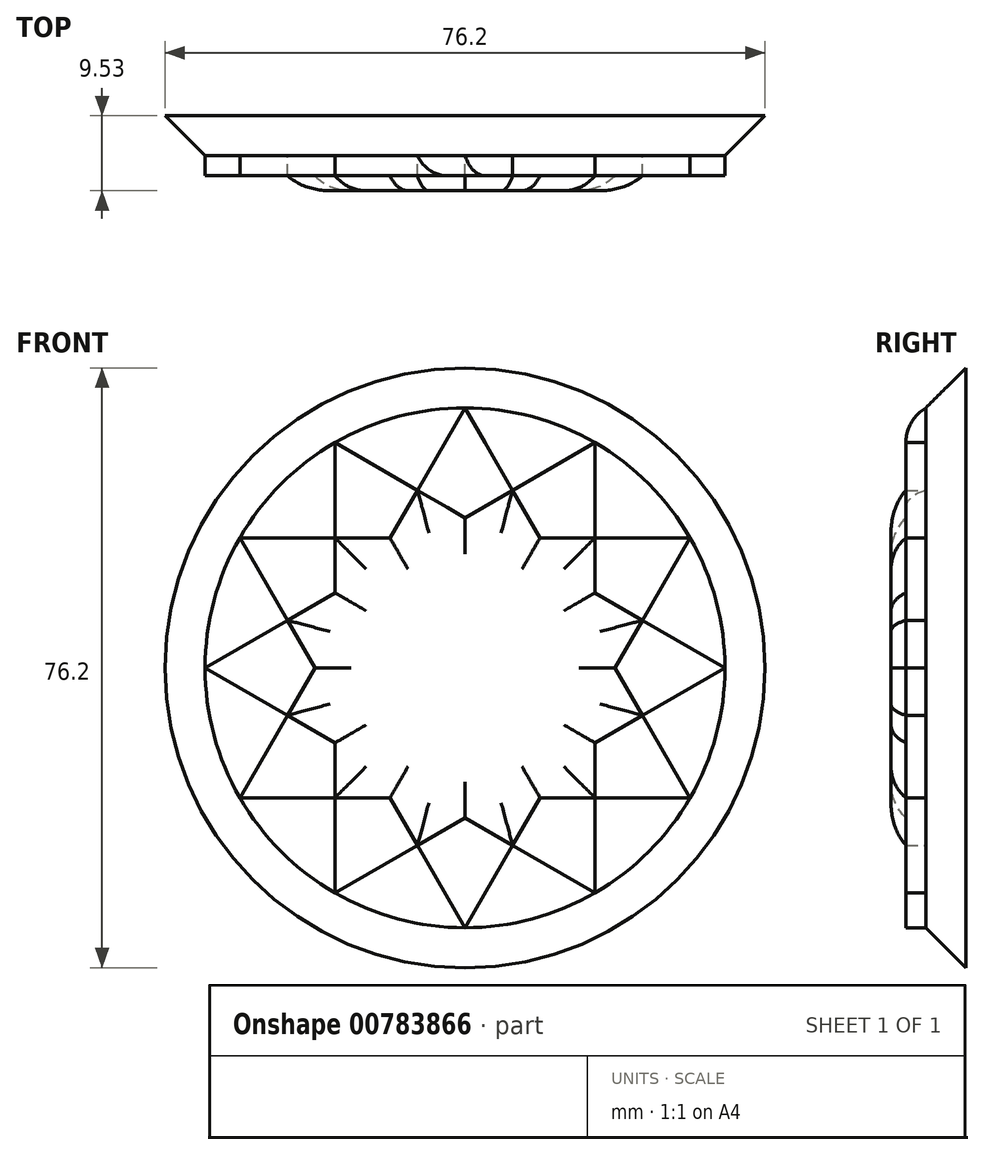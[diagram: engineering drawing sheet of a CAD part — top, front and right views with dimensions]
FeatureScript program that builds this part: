
annotation { "Feature Type Name" : "Feature", "Feature Type Description" : "" }
export const myFeature = defineFeature(function(context is Context, id is Id, definition is map)
    precondition{}
    {
        {
            var Q0;
            Q0=qCreatedBy(makeId("Front.planeOp"),FACE);
            var sketch = newSketch(context, id + "F0", { "sketchPlane" : qUnion([Q0])});
            skCircle(sketch, "E0", {"center": v(0, 0) * mm, "radius": 38.1 * mm});
            skSolve(sketch);
        }
        {
            var Q0;
            Q0=makeQuery(id+"F0.imprint","IMPRINT",FACE,{"disambiguationData":[TD([[makeQuery(id+"F0.imprint","IMPRINT",EDGE,{"derivedFrom":sQuery(id+"F0.wireOp",EDGE,"E0")}),1.0]])]});
            extrude(context, id + "F1", {"entities" : qUnion([Q0]), "depth" : 5.08 * mm, "offsetDistance" : 25.4 * mm});
        }
        {
            var Q0;
            Q0=makeQuery(id+"F1.opExtrude","CAP_EDGE",EDGE,{"disambiguationData":[OSD([sQuery(id+"F0.wireOp",EDGE,"E0")])],"isStart":false});
            chamfer(context, id + "F2", {"entities" : qUnion([Q0]), "width" : 5.08 * mm, "tangentPropagation" : true});
        }
        {
            var Q0;
            Q0=makeQuery(id+"F1.opExtrude","CAP_FACE",FACE,{"disambiguationData":[OSD([sQuery(id+"F0.wireOp",EDGE,"E0")])],"isStart":false});
            var sketch = newSketch(context, id + "F3", { "sketchPlane" : qUnion([Q0])});
            skCircle(sketch, "E1.cCircle", {"center": v(0, 0) * mm, "radius": 33.02 * mm, "construction": true});
            skLineSegment(sketch, "E1.0", {"start": v(0, 33.02) * mm, "end": v(28.6, -16.5) * mm});
            skLineSegment(sketch, "E1.1", {"start": v(28.6, -16.5) * mm, "end": v(-28.6, -16.51) * mm});
            skLineSegment(sketch, "E1.2", {"start": v(-28.6, -16.51) * mm, "end": v(0, 33.02) * mm});
            skLineSegment(sketch, "E2.0", {"start": v(-28.6, 16.5) * mm, "end": v(28.6, 16.52) * mm});
            skLineSegment(sketch, "E2.1", {"start": v(28.6, 16.52) * mm, "end": v(0, -33.02) * mm});
            skLineSegment(sketch, "E2.2", {"start": v(0, -33.02) * mm, "end": v(-28.6, 16.5) * mm});
            skLineSegment(sketch, "E3.0", {"start": v(-33.02, 0) * mm, "end": v(16.5, 28.6) * mm});
            skLineSegment(sketch, "E3.1", {"start": v(16.5, 28.6) * mm, "end": v(16.51, -28.6) * mm});
            skLineSegment(sketch, "E3.2", {"start": v(16.5, -28.6) * mm, "end": v(-33.02, 0) * mm});
            skLineSegment(sketch, "E4.0", {"start": v(33.02, 0) * mm, "end": v(-16.5, -28.6) * mm});
            skLineSegment(sketch, "E4.1", {"start": v(-16.5, -28.6) * mm, "end": v(-16.51, 28.6) * mm});
            skLineSegment(sketch, "E4.2", {"start": v(-16.51, 28.6) * mm, "end": v(33.02, 0) * mm});
            skSolve(sketch);
        }
        {
            var Q0;
            {var subQ0=sQuery(id+"F3.wireOp",EDGE,"E3.2");var subQ1=sQuery(id+"F3.wireOp",EDGE,"E2.2");var subQ2=makeQuery(id+"F3.imprint","INTERSECT",VERTEX,{"derivedFrom":[subQ1,subQ0]});Q0=makeQuery(id+"F3.imprint","IMPRINT",FACE,{"disambiguationData":[TD([[makeQuery(id+"F3.imprint","IMPRINT",EDGE,{"disambiguationData":[TD([[subQ2,-1.0]])],"derivedFrom":subQ1}),1.0]])]});}
            var Q1;
            {var subQ0=sQuery(id+"F3.wireOp",EDGE,"E3.2");var subQ1=sQuery(id+"F3.wireOp",EDGE,"E1.2");var subQ2=makeQuery(id+"F3.imprint","INTERSECT",VERTEX,{"derivedFrom":[subQ1,subQ0]});Q1=makeQuery(id+"F3.imprint","IMPRINT",FACE,{"disambiguationData":[TD([[makeQuery(id+"F3.imprint","IMPRINT",EDGE,{"disambiguationData":[TD([[subQ2,-1.0]])],"derivedFrom":subQ1}),-1.0]])]});}
            var Q2;
            {var subQ0=sQuery(id+"F3.wireOp",EDGE,"E2.2");var subQ1=sQuery(id+"F3.wireOp",EDGE,"E1.1");var subQ2=makeQuery(id+"F3.imprint","INTERSECT",VERTEX,{"derivedFrom":[subQ1,subQ0]});Q2=makeQuery(id+"F3.imprint","IMPRINT",FACE,{"disambiguationData":[TD([[makeQuery(id+"F3.imprint","IMPRINT",EDGE,{"disambiguationData":[TD([[subQ2,-1.0]])],"derivedFrom":subQ1}),-1.0]])]});}
            var Q3;
            {var subQ0=sQuery(id+"F3.wireOp",EDGE,"E2.2");var subQ1=sQuery(id+"F3.wireOp",EDGE,"E1.2");var subQ2=makeQuery(id+"F3.imprint","INTERSECT",VERTEX,{"derivedFrom":[subQ1,subQ0]});Q3=makeQuery(id+"F3.imprint","IMPRINT",FACE,{"disambiguationData":[TD([[makeQuery(id+"F3.imprint","IMPRINT",EDGE,{"disambiguationData":[TD([[subQ2,-1.0]])],"derivedFrom":subQ1}),-1.0]])]});}
            var Q4;
            {var subQ0=sQuery(id+"F3.wireOp",EDGE,"E2.2");var subQ1=sQuery(id+"F3.wireOp",EDGE,"E1.2");var subQ2=makeQuery(id+"F3.imprint","INTERSECT",VERTEX,{"derivedFrom":[subQ1,subQ0]});Q4=makeQuery(id+"F3.imprint","IMPRINT",FACE,{"disambiguationData":[TD([[makeQuery(id+"F3.imprint","IMPRINT",EDGE,{"disambiguationData":[TD([[subQ2,-1.0]])],"derivedFrom":subQ1}),1.0]])]});}
            var Q5;
            {var subQ0=sQuery(id+"F3.wireOp",EDGE,"E3.0");var subQ1=sQuery(id+"F3.wireOp",EDGE,"E1.2");var subQ2=makeQuery(id+"F3.imprint","INTERSECT",VERTEX,{"derivedFrom":[subQ1,subQ0]});Q5=makeQuery(id+"F3.imprint","IMPRINT",FACE,{"disambiguationData":[TD([[makeQuery(id+"F3.imprint","IMPRINT",EDGE,{"disambiguationData":[TD([[subQ2,-1.0]])],"derivedFrom":subQ1}),1.0]])]});}
            var Q6;
            {var subQ0=sQuery(id+"F3.wireOp",EDGE,"E3.0");var subQ1=sQuery(id+"F3.wireOp",EDGE,"E1.2");var subQ2=makeQuery(id+"F3.imprint","INTERSECT",VERTEX,{"derivedFrom":[subQ1,subQ0]});Q6=makeQuery(id+"F3.imprint","IMPRINT",FACE,{"disambiguationData":[TD([[makeQuery(id+"F3.imprint","IMPRINT",EDGE,{"disambiguationData":[TD([[subQ2,-1.0]])],"derivedFrom":subQ1}),-1.0]])]});}
            var Q7;
            {var subQ0=sQuery(id+"F3.wireOp",EDGE,"E4.1");var subQ1=sQuery(id+"F3.wireOp",EDGE,"E1.2");var subQ2=makeQuery(id+"F3.imprint","INTERSECT",VERTEX,{"derivedFrom":[subQ1,subQ0]});Q7=makeQuery(id+"F3.imprint","IMPRINT",FACE,{"disambiguationData":[TD([[makeQuery(id+"F3.imprint","IMPRINT",EDGE,{"disambiguationData":[TD([[subQ2,-1.0]])],"derivedFrom":subQ1}),1.0]])]});}
            var Q8;
            {var subQ10=sQuery(id+"F3.wireOp",EDGE,"E1.0");var subQ20=sQuery(id+"F3.wireOp",EDGE,"E4.2");var subQ21=makeQuery(id+"F3.imprint","INTERSECT",VERTEX,{"derivedFrom":[subQ10,subQ20]});Q8=makeQuery(id+"F3.imprint","IMPRINT",FACE,{"disambiguationData":[TD([[makeQuery(id+"F3.imprint","IMPRINT",EDGE,{"disambiguationData":[TD([[subQ21,-1.0]])],"derivedFrom":subQ10}),-1.0]])]});}
            var Q9;
            {var subQ0=sQuery(id+"F3.wireOp",EDGE,"E2.0");var subQ1=sQuery(id+"F3.wireOp",EDGE,"E1.2");var subQ2=makeQuery(id+"F3.imprint","INTERSECT",VERTEX,{"derivedFrom":[subQ1,subQ0]});Q9=makeQuery(id+"F3.imprint","IMPRINT",FACE,{"disambiguationData":[TD([[makeQuery(id+"F3.imprint","IMPRINT",EDGE,{"disambiguationData":[TD([[subQ2,-1.0]])],"derivedFrom":subQ1}),-1.0]])]});}
            var Q10;
            {var subQ0=sQuery(id+"F3.wireOp",EDGE,"E3.0");var subQ1=sQuery(id+"F3.wireOp",EDGE,"E2.0");var subQ2=makeQuery(id+"F3.imprint","INTERSECT",VERTEX,{"derivedFrom":[subQ1,subQ0]});Q10=makeQuery(id+"F3.imprint","IMPRINT",FACE,{"disambiguationData":[TD([[makeQuery(id+"F3.imprint","IMPRINT",EDGE,{"disambiguationData":[TD([[subQ2,-1.0]])],"derivedFrom":subQ1}),1.0]])]});}
            var Q11;
            {var subQ0=sQuery(id+"F3.wireOp",EDGE,"E3.0");var subQ1=sQuery(id+"F3.wireOp",EDGE,"E1.0");var subQ2=makeQuery(id+"F3.imprint","INTERSECT",VERTEX,{"derivedFrom":[subQ1,subQ0]});Q11=makeQuery(id+"F3.imprint","IMPRINT",FACE,{"disambiguationData":[TD([[makeQuery(id+"F3.imprint","IMPRINT",EDGE,{"disambiguationData":[TD([[subQ2,-1.0]])],"derivedFrom":subQ1}),-1.0]])]});}
            var Q12;
            {var subQ0=sQuery(id+"F3.wireOp",EDGE,"E2.0");var subQ1=sQuery(id+"F3.wireOp",EDGE,"E1.0");var subQ2=makeQuery(id+"F3.imprint","INTERSECT",VERTEX,{"derivedFrom":[subQ1,subQ0]});Q12=makeQuery(id+"F3.imprint","IMPRINT",FACE,{"disambiguationData":[TD([[makeQuery(id+"F3.imprint","IMPRINT",EDGE,{"disambiguationData":[TD([[subQ2,-1.0]])],"derivedFrom":subQ1}),-1.0]])]});}
            var Q13;
            {var subQ0=sQuery(id+"F3.wireOp",EDGE,"E4.2");var subQ1=sQuery(id+"F3.wireOp",EDGE,"E1.0");var subQ2=makeQuery(id+"F3.imprint","INTERSECT",VERTEX,{"derivedFrom":[subQ1,subQ0]});Q13=makeQuery(id+"F3.imprint","IMPRINT",FACE,{"disambiguationData":[TD([[makeQuery(id+"F3.imprint","IMPRINT",EDGE,{"disambiguationData":[TD([[subQ2,-1.0]])],"derivedFrom":subQ1}),1.0]])]});}
            var Q14;
            {var subQ0=sQuery(id+"F3.wireOp",EDGE,"E3.1");var subQ1=sQuery(id+"F3.wireOp",EDGE,"E1.0");var subQ2=makeQuery(id+"F3.imprint","INTERSECT",VERTEX,{"derivedFrom":[subQ1,subQ0]});Q14=makeQuery(id+"F3.imprint","IMPRINT",FACE,{"disambiguationData":[TD([[makeQuery(id+"F3.imprint","IMPRINT",EDGE,{"disambiguationData":[TD([[subQ2,-1.0]])],"derivedFrom":subQ1}),1.0]])]});}
            var Q15;
            {var subQ0=sQuery(id+"F3.wireOp",EDGE,"E2.0");var subQ1=sQuery(id+"F3.wireOp",EDGE,"E1.0");var subQ2=makeQuery(id+"F3.imprint","INTERSECT",VERTEX,{"derivedFrom":[subQ1,subQ0]});Q15=makeQuery(id+"F3.imprint","IMPRINT",FACE,{"disambiguationData":[TD([[makeQuery(id+"F3.imprint","IMPRINT",EDGE,{"disambiguationData":[TD([[subQ2,-1.0]])],"derivedFrom":subQ1}),1.0]])]});}
            var Q16;
            {var subQ0=sQuery(id+"F3.wireOp",EDGE,"E3.1");var subQ1=sQuery(id+"F3.wireOp",EDGE,"E1.0");var subQ2=makeQuery(id+"F3.imprint","INTERSECT",VERTEX,{"derivedFrom":[subQ1,subQ0]});Q16=makeQuery(id+"F3.imprint","IMPRINT",FACE,{"disambiguationData":[TD([[makeQuery(id+"F3.imprint","IMPRINT",EDGE,{"disambiguationData":[TD([[subQ2,-1.0]])],"derivedFrom":subQ1}),-1.0]])]});}
            var Q17;
            {var subQ0=sQuery(id+"F3.wireOp",EDGE,"E2.1");var subQ1=sQuery(id+"F3.wireOp",EDGE,"E1.0");var subQ2=makeQuery(id+"F3.imprint","INTERSECT",VERTEX,{"derivedFrom":[subQ1,subQ0]});Q17=makeQuery(id+"F3.imprint","IMPRINT",FACE,{"disambiguationData":[TD([[makeQuery(id+"F3.imprint","IMPRINT",EDGE,{"disambiguationData":[TD([[subQ2,-1.0]])],"derivedFrom":subQ1}),-1.0]])]});}
            var Q18;
            {var subQ0=sQuery(id+"F3.wireOp",EDGE,"E3.1");var subQ1=sQuery(id+"F3.wireOp",EDGE,"E2.1");var subQ2=makeQuery(id+"F3.imprint","INTERSECT",VERTEX,{"derivedFrom":[subQ1,subQ0]});Q18=makeQuery(id+"F3.imprint","IMPRINT",FACE,{"disambiguationData":[TD([[makeQuery(id+"F3.imprint","IMPRINT",EDGE,{"disambiguationData":[TD([[subQ2,-1.0]])],"derivedFrom":subQ1}),1.0]])]});}
            var Q19;
            {var subQ0=sQuery(id+"F3.wireOp",EDGE,"E3.1");var subQ1=sQuery(id+"F3.wireOp",EDGE,"E1.1");var subQ2=makeQuery(id+"F3.imprint","INTERSECT",VERTEX,{"derivedFrom":[subQ1,subQ0]});Q19=makeQuery(id+"F3.imprint","IMPRINT",FACE,{"disambiguationData":[TD([[makeQuery(id+"F3.imprint","IMPRINT",EDGE,{"disambiguationData":[TD([[subQ2,-1.0]])],"derivedFrom":subQ1}),-1.0]])]});}
            var Q20;
            {var subQ0=sQuery(id+"F3.wireOp",EDGE,"E2.1");var subQ1=sQuery(id+"F3.wireOp",EDGE,"E1.1");var subQ2=makeQuery(id+"F3.imprint","INTERSECT",VERTEX,{"derivedFrom":[subQ1,subQ0]});Q20=makeQuery(id+"F3.imprint","IMPRINT",FACE,{"disambiguationData":[TD([[makeQuery(id+"F3.imprint","IMPRINT",EDGE,{"disambiguationData":[TD([[subQ2,-1.0]])],"derivedFrom":subQ1}),1.0]])]});}
            var Q21;
            {var subQ0=sQuery(id+"F3.wireOp",EDGE,"E2.1");var subQ1=sQuery(id+"F3.wireOp",EDGE,"E1.1");var subQ2=makeQuery(id+"F3.imprint","INTERSECT",VERTEX,{"derivedFrom":[subQ1,subQ0]});Q21=makeQuery(id+"F3.imprint","IMPRINT",FACE,{"disambiguationData":[TD([[makeQuery(id+"F3.imprint","IMPRINT",EDGE,{"disambiguationData":[TD([[subQ2,-1.0]])],"derivedFrom":subQ1}),-1.0]])]});}
            var Q22;
            {var subQ0=sQuery(id+"F3.wireOp",EDGE,"E3.2");var subQ1=sQuery(id+"F3.wireOp",EDGE,"E1.1");var subQ2=makeQuery(id+"F3.imprint","INTERSECT",VERTEX,{"derivedFrom":[subQ1,subQ0]});Q22=makeQuery(id+"F3.imprint","IMPRINT",FACE,{"disambiguationData":[TD([[makeQuery(id+"F3.imprint","IMPRINT",EDGE,{"disambiguationData":[TD([[subQ2,-1.0]])],"derivedFrom":subQ1}),1.0]])]});}
            var Q23;
            {var subQ0=sQuery(id+"F3.wireOp",EDGE,"E3.2");var subQ1=sQuery(id+"F3.wireOp",EDGE,"E1.1");var subQ2=makeQuery(id+"F3.imprint","INTERSECT",VERTEX,{"derivedFrom":[subQ1,subQ0]});Q23=makeQuery(id+"F3.imprint","IMPRINT",FACE,{"disambiguationData":[TD([[makeQuery(id+"F3.imprint","IMPRINT",EDGE,{"disambiguationData":[TD([[subQ2,-1.0]])],"derivedFrom":subQ1}),-1.0]])]});}
            var Q24;
            {var subQ0=sQuery(id+"F3.wireOp",EDGE,"E4.0");var subQ1=sQuery(id+"F3.wireOp",EDGE,"E1.1");var subQ2=makeQuery(id+"F3.imprint","INTERSECT",VERTEX,{"derivedFrom":[subQ1,subQ0]});Q24=makeQuery(id+"F3.imprint","IMPRINT",FACE,{"disambiguationData":[TD([[makeQuery(id+"F3.imprint","IMPRINT",EDGE,{"disambiguationData":[TD([[subQ2,-1.0]])],"derivedFrom":subQ1}),1.0]])]});}
            extrude(context, id + "F4", {"entities" : qUnion([Q0, Q1, Q2, Q3, Q4, Q5, Q6, Q7, Q8, Q9, Q10, Q11, Q12, Q13, Q14, Q15, Q16, Q17, Q18, Q19, Q20, Q21, Q22, Q23, Q24]), "operationType" : NewBodyOperationType.ADD, "depth" : 4.44 * mm, "offsetDistance" : 25.4 * mm});
        }
        {
            var Q0;
            Q0 = qSketchRegion(id + "F3", true);
            extrude(context, id + "F5", {"entities" : qUnion([Q0]), "operationType" : NewBodyOperationType.ADD, "depth" : 2.54 * mm, "offsetDistance" : 25.4 * mm});
        }
        {
            var Q0;
            Q0=makeQuery(id+"F4.opExtrude","CAP_FACE",FACE,{"disambiguationData":[OSD([sQuery(id+"F3.wireOp",EDGE,"E1.0"),sQuery(id+"F3.wireOp",EDGE,"E1.1"),sQuery(id+"F3.wireOp",EDGE,"E1.2"),sQuery(id+"F3.wireOp",EDGE,"E2.0"),sQuery(id+"F3.wireOp",EDGE,"E2.1"),sQuery(id+"F3.wireOp",EDGE,"E2.2"),sQuery(id+"F3.wireOp",EDGE,"E3.0"),sQuery(id+"F3.wireOp",EDGE,"E3.1"),sQuery(id+"F3.wireOp",EDGE,"E3.2"),sQuery(id+"F3.wireOp",EDGE,"E4.0"),sQuery(id+"F3.wireOp",EDGE,"E4.1"),sQuery(id+"F3.wireOp",EDGE,"E4.2")])],"isStart":false});
            fillet(context, id + "F6", {"entities" : qUnion([Q0]), "radius" : 5.08 * mm, "tangentPropagation" : true, "allowEdgeOverflow" : false});
        }
        {
            var Q0;
            {var subQ0=sQuery(id+"F3.wireOp",EDGE,"E1.2");Q0=makeQuery(id+"F5.opExtrude","CAP_EDGE",EDGE,{"disambiguationData":[OSD([subQ0]),TDD([makeQuery(id+"F3.imprint","IMPRINT",EDGE,{"disambiguationData":[TD([[makeQuery(id+"F3.imprint","INTERSECT",VERTEX,{"derivedFrom":[subQ0,sQuery(id+"F3.wireOp",EDGE,"E4.2")]}),-1.0]])],"derivedFrom":subQ0})])],"isStart":false});}
            fillet(context, id + "F7", {"entities" : qUnion([Q0]), "radius" : 5.08 * mm, "tangentPropagation" : true, "allowEdgeOverflow" : false});
        }
    });
